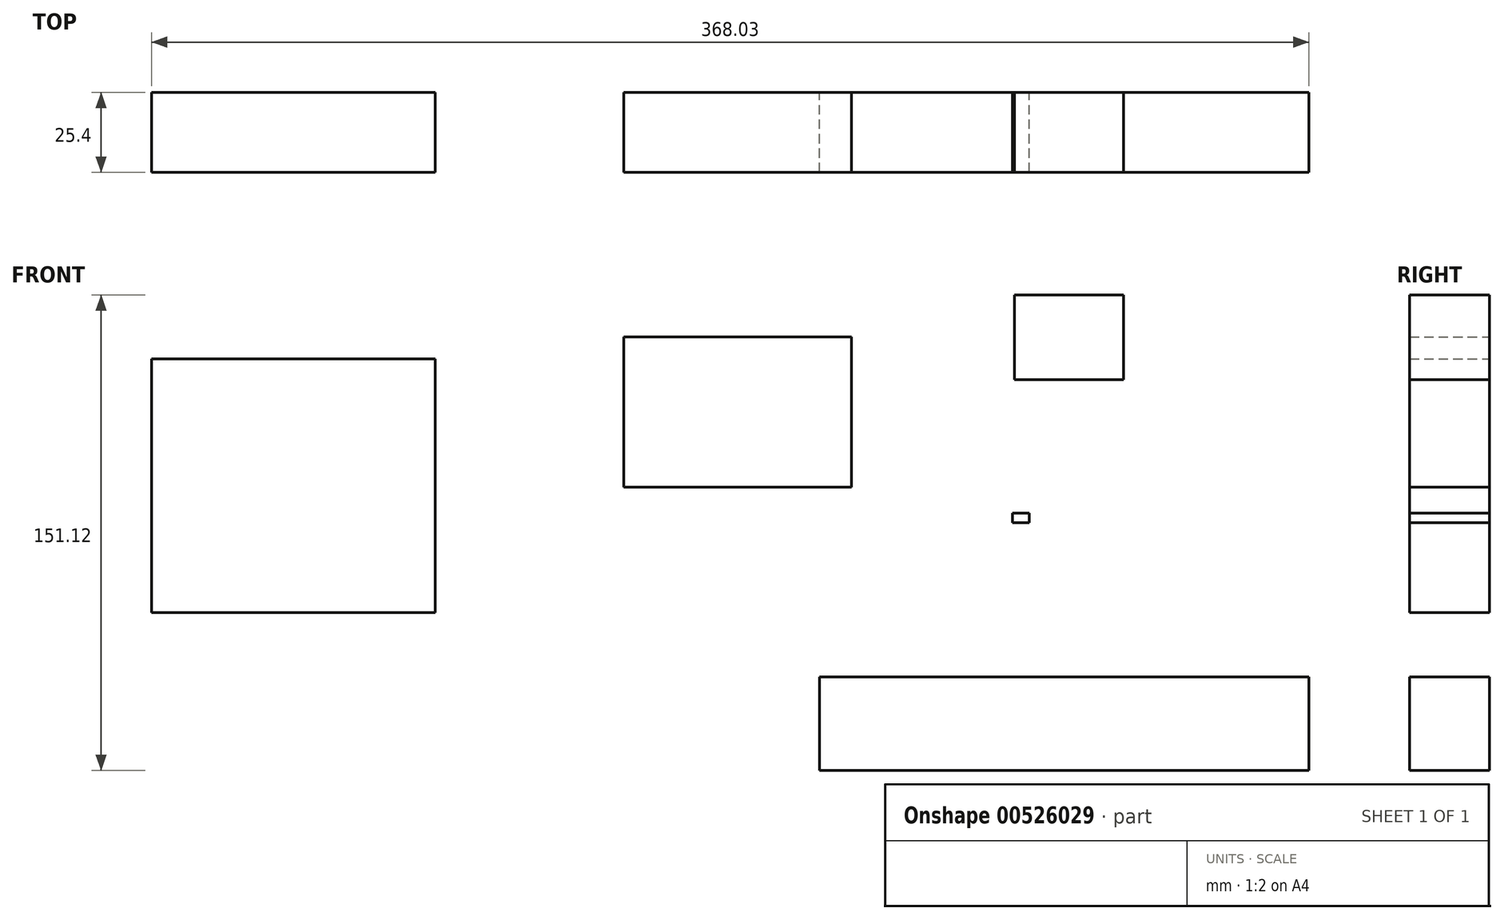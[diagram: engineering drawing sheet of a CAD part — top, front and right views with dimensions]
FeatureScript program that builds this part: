
annotation { "Feature Type Name" : "Feature", "Feature Type Description" : "" }
export const myFeature = defineFeature(function(context is Context, id is Id, definition is map)
    precondition{}
    {
        {
            var Q0;
            Q0=qCreatedBy(makeId("Front.planeOp"),FACE);
            var sketch = newSketch(context, id + "F0", { "sketchPlane" : qUnion([Q0])});
            skLineSegment(sketch, "E0.bottom", {"start": v(-88.67, 29.13) * mm, "end": v(-16.22, 29.13) * mm});
            skLineSegment(sketch, "E0.top", {"start": v(-88.67, -18.62) * mm, "end": v(-16.22, -18.62) * mm});
            skLineSegment(sketch, "E0.left", {"start": v(-88.67, 29.13) * mm, "end": v(-88.67, -18.62) * mm});
            skLineSegment(sketch, "E0.right", {"start": v(-16.22, 29.13) * mm, "end": v(-16.22, -18.62) * mm});
            skLineSegment(sketch, "E1.bottom", {"start": v(35.58, 42.4) * mm, "end": v(70.24, 42.4) * mm});
            skLineSegment(sketch, "E1.top", {"start": v(35.58, 15.49) * mm, "end": v(70.24, 15.49) * mm});
            skLineSegment(sketch, "E1.left", {"start": v(35.58, 42.4) * mm, "end": v(35.58, 15.49) * mm});
            skLineSegment(sketch, "E1.right", {"start": v(70.24, 42.4) * mm, "end": v(70.24, 15.49) * mm});
            skLineSegment(sketch, "E2.bottom", {"start": v(-238.83, 22.12) * mm, "end": v(-148.6, 22.12) * mm});
            skLineSegment(sketch, "E2.top", {"start": v(-238.83, -58.49) * mm, "end": v(-148.6, -58.49) * mm});
            skLineSegment(sketch, "E2.left", {"start": v(-238.83, 22.12) * mm, "end": v(-238.83, -58.49) * mm});
            skLineSegment(sketch, "E2.right", {"start": v(-148.6, 22.12) * mm, "end": v(-148.6, -58.49) * mm});
            skLineSegment(sketch, "E3.bottom", {"start": v(34.94, -26.86) * mm, "end": v(40.21, -26.86) * mm});
            skLineSegment(sketch, "E3.top", {"start": v(34.94, -29.96) * mm, "end": v(40.21, -29.96) * mm});
            skLineSegment(sketch, "E3.left", {"start": v(34.94, -26.86) * mm, "end": v(34.94, -29.96) * mm});
            skLineSegment(sketch, "E3.right", {"start": v(40.21, -26.86) * mm, "end": v(40.21, -29.96) * mm});
            skLineSegment(sketch, "E4.bottom", {"start": v(129.2, -78.95) * mm, "end": v(-26.45, -78.95) * mm});
            skLineSegment(sketch, "E4.top", {"start": v(129.2, -108.72) * mm, "end": v(-26.45, -108.72) * mm});
            skLineSegment(sketch, "E4.left", {"start": v(129.2, -78.95) * mm, "end": v(129.2, -108.72) * mm});
            skLineSegment(sketch, "E4.right", {"start": v(-26.45, -78.95) * mm, "end": v(-26.45, -108.72) * mm});
            skSolve(sketch);
        }
        {
            var Q0;
            Q0 = qSketchRegion(id + "F0", true);
            extrude(context, id + "F1", {"entities" : qUnion([Q0]), "depth" : 25.4 * mm, "offsetDistance" : 25.4 * mm});
        }
    });
